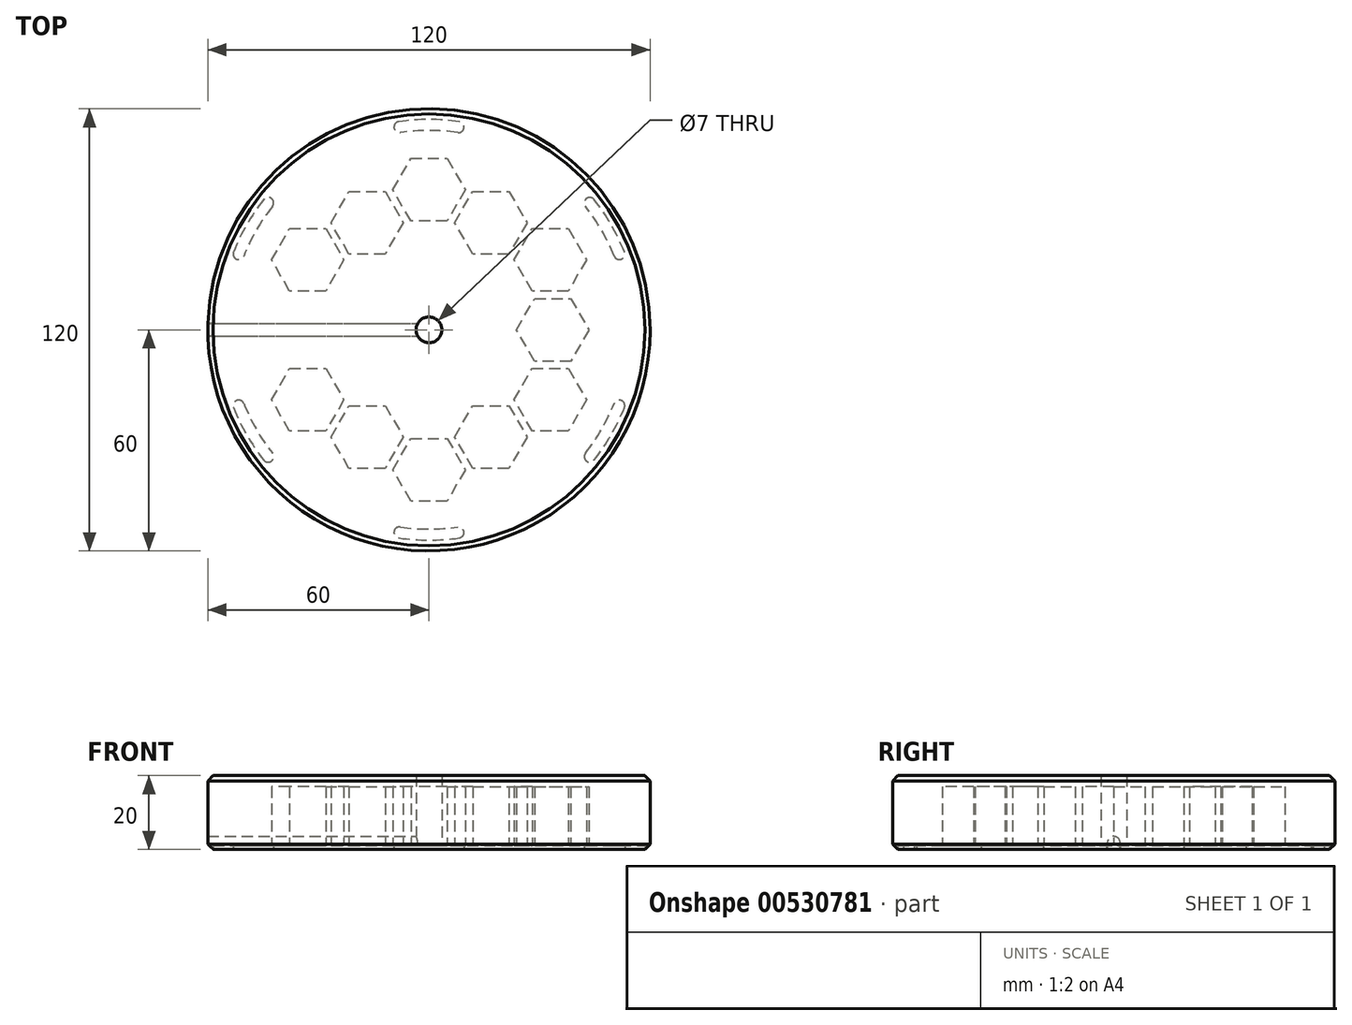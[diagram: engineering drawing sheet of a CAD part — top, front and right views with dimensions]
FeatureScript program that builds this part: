
annotation { "Feature Type Name" : "Feature", "Feature Type Description" : "" }
export const myFeature = defineFeature(function(context is Context, id is Id, definition is map)
    precondition{}
    {
        {
            var Q0;
            Q0=qCreatedBy(makeId("Top.planeOp"),FACE);
            var sketch = newSketch(context, id + "F0", { "sketchPlane" : qUnion([Q0])});
            skCircle(sketch, "E0", {"center": v(0, 0) * mm, "radius": 60 * mm});
            skCircle(sketch, "E1.cCircle", {"center": v(0, 38) * mm, "radius": 8.5 * mm, "construction": true});
            skLineSegment(sketch, "E1.0", {"start": v(4.9, 29.5) * mm, "end": v(-4.9, 29.5) * mm});
            skLineSegment(sketch, "E1.1", {"start": v(-4.9, 29.5) * mm, "end": v(-9.81, 38) * mm});
            skLineSegment(sketch, "E1.2", {"start": v(-9.81, 38) * mm, "end": v(-4.9, 46.5) * mm});
            skLineSegment(sketch, "E1.3", {"start": v(-4.9, 46.5) * mm, "end": v(4.9, 46.5) * mm});
            skLineSegment(sketch, "E1.4", {"start": v(4.9, 46.5) * mm, "end": v(9.81, 38) * mm});
            skLineSegment(sketch, "E1.5", {"start": v(9.81, 38) * mm, "end": v(4.9, 29.5) * mm});
            skPoint(sketch, "E1.0.midPoint", {"position": v(0, 29.5) * mm});
            skLineSegment(sketch, "E2.1.0", {"start": v(-28, 10.5) * mm, "end": v(-37.82, 10.5) * mm});
            skLineSegment(sketch, "E2.1.1", {"start": v(-37.82, 10.5) * mm, "end": v(-42.72, 19) * mm});
            skLineSegment(sketch, "E2.1.2", {"start": v(-42.72, 19) * mm, "end": v(-37.82, 27.5) * mm});
            skLineSegment(sketch, "E2.1.3", {"start": v(-37.82, 27.5) * mm, "end": v(-28, 27.5) * mm});
            skLineSegment(sketch, "E2.1.4", {"start": v(-28, 27.5) * mm, "end": v(-23.1, 19) * mm});
            skLineSegment(sketch, "E2.1.5", {"start": v(-23.1, 19) * mm, "end": v(-28, 10.5) * mm});
            skLineSegment(sketch, "E2.2.0", {"start": v(-23.1, -19) * mm, "end": v(-28, -27.5) * mm});
            skLineSegment(sketch, "E2.2.1", {"start": v(-28, -27.5) * mm, "end": v(-37.82, -27.5) * mm});
            skLineSegment(sketch, "E2.2.2", {"start": v(-37.82, -27.5) * mm, "end": v(-42.72, -19) * mm});
            skLineSegment(sketch, "E2.2.3", {"start": v(-42.72, -19) * mm, "end": v(-37.82, -10.5) * mm});
            skLineSegment(sketch, "E2.2.4", {"start": v(-37.82, -10.5) * mm, "end": v(-28, -10.5) * mm});
            skLineSegment(sketch, "E2.2.5", {"start": v(-28, -10.5) * mm, "end": v(-23.1, -19) * mm});
            skLineSegment(sketch, "E2.3.0", {"start": v(4.9, -29.5) * mm, "end": v(9.81, -38) * mm});
            skLineSegment(sketch, "E2.3.1", {"start": v(9.81, -38) * mm, "end": v(4.9, -46.5) * mm});
            skLineSegment(sketch, "E2.3.2", {"start": v(4.9, -46.5) * mm, "end": v(-4.9, -46.5) * mm});
            skLineSegment(sketch, "E2.3.3", {"start": v(-4.9, -46.5) * mm, "end": v(-9.81, -38) * mm});
            skLineSegment(sketch, "E2.3.4", {"start": v(-9.81, -38) * mm, "end": v(-4.9, -29.5) * mm});
            skLineSegment(sketch, "E2.3.5", {"start": v(-4.9, -29.5) * mm, "end": v(4.9, -29.5) * mm});
            skLineSegment(sketch, "E2.4.0", {"start": v(28, -10.5) * mm, "end": v(37.82, -10.5) * mm});
            skLineSegment(sketch, "E2.4.1", {"start": v(37.82, -10.5) * mm, "end": v(42.72, -19) * mm});
            skLineSegment(sketch, "E2.4.2", {"start": v(42.72, -19) * mm, "end": v(37.82, -27.5) * mm});
            skLineSegment(sketch, "E2.4.3", {"start": v(37.82, -27.5) * mm, "end": v(28, -27.5) * mm});
            skLineSegment(sketch, "E2.4.4", {"start": v(28, -27.5) * mm, "end": v(23.1, -19) * mm});
            skLineSegment(sketch, "E2.4.5", {"start": v(23.1, -19) * mm, "end": v(28, -10.5) * mm});
            skLineSegment(sketch, "E2.5.0", {"start": v(23.1, 19) * mm, "end": v(28, 27.5) * mm});
            skLineSegment(sketch, "E2.5.1", {"start": v(28, 27.5) * mm, "end": v(37.82, 27.5) * mm});
            skLineSegment(sketch, "E2.5.2", {"start": v(37.82, 27.5) * mm, "end": v(42.72, 19) * mm});
            skLineSegment(sketch, "E2.5.3", {"start": v(42.72, 19) * mm, "end": v(37.82, 10.5) * mm});
            skLineSegment(sketch, "E2.5.4", {"start": v(37.82, 10.5) * mm, "end": v(28, 10.5) * mm});
            skLineSegment(sketch, "E2.5.5", {"start": v(28, 10.5) * mm, "end": v(23.1, 19) * mm});
            skCircle(sketch, "E3", {"center": v(0, 0) * mm, "radius": 3.5 * mm});
            skCircle(sketch, "E4.cCircle", {"center": v(-16.79, 29.08) * mm, "radius": 8.5 * mm, "construction": true});
            skLineSegment(sketch, "E4.0", {"start": v(-21.7, 37.58) * mm, "end": v(-11.88, 37.58) * mm});
            skLineSegment(sketch, "E4.1", {"start": v(-11.88, 37.58) * mm, "end": v(-6.97, 29.08) * mm});
            skLineSegment(sketch, "E4.2", {"start": v(-6.97, 29.08) * mm, "end": v(-11.88, 20.58) * mm});
            skLineSegment(sketch, "E4.3", {"start": v(-11.88, 20.58) * mm, "end": v(-21.7, 20.58) * mm});
            skLineSegment(sketch, "E4.4", {"start": v(-21.7, 20.58) * mm, "end": v(-26.6, 29.08) * mm});
            skLineSegment(sketch, "E4.5", {"start": v(-26.6, 29.08) * mm, "end": v(-21.7, 37.58) * mm});
            skPoint(sketch, "E4.0.midPoint", {"position": v(-16.79, 37.58) * mm});
            skLineSegment(sketch, "E5.1.0", {"start": v(11.88, 20.58) * mm, "end": v(6.97, 29.08) * mm});
            skLineSegment(sketch, "E5.1.1", {"start": v(21.7, 20.58) * mm, "end": v(11.88, 20.58) * mm});
            skLineSegment(sketch, "E5.1.2", {"start": v(26.6, 29.08) * mm, "end": v(21.7, 20.58) * mm});
            skLineSegment(sketch, "E5.1.3", {"start": v(21.7, 37.58) * mm, "end": v(26.6, 29.08) * mm});
            skLineSegment(sketch, "E5.1.4", {"start": v(11.88, 37.58) * mm, "end": v(21.7, 37.58) * mm});
            skLineSegment(sketch, "E5.1.5", {"start": v(6.97, 29.08) * mm, "end": v(11.88, 37.58) * mm});
            skLineSegment(sketch, "E5.2.0", {"start": v(23.76, 0) * mm, "end": v(28.67, 8.5) * mm});
            skLineSegment(sketch, "E5.2.1", {"start": v(28.67, -8.5) * mm, "end": v(23.76, 0) * mm});
            skLineSegment(sketch, "E5.2.2", {"start": v(38.49, -8.5) * mm, "end": v(28.67, -8.5) * mm});
            skLineSegment(sketch, "E5.2.3", {"start": v(43.4, 0) * mm, "end": v(38.49, -8.5) * mm});
            skLineSegment(sketch, "E5.2.4", {"start": v(38.49, 8.5) * mm, "end": v(43.4, 0) * mm});
            skLineSegment(sketch, "E5.2.5", {"start": v(28.67, 8.5) * mm, "end": v(38.49, 8.5) * mm});
            skLineSegment(sketch, "E5.3.0", {"start": v(11.88, -20.58) * mm, "end": v(21.7, -20.58) * mm});
            skLineSegment(sketch, "E5.3.1", {"start": v(6.97, -29.08) * mm, "end": v(11.88, -20.58) * mm});
            skLineSegment(sketch, "E5.3.2", {"start": v(11.88, -37.58) * mm, "end": v(6.97, -29.08) * mm});
            skLineSegment(sketch, "E5.3.3", {"start": v(21.7, -37.58) * mm, "end": v(11.88, -37.58) * mm});
            skLineSegment(sketch, "E5.3.4", {"start": v(26.6, -29.08) * mm, "end": v(21.7, -37.58) * mm});
            skLineSegment(sketch, "E5.3.5", {"start": v(21.7, -20.58) * mm, "end": v(26.6, -29.08) * mm});
            skLineSegment(sketch, "E5.4.0", {"start": v(-11.88, -20.58) * mm, "end": v(-6.97, -29.08) * mm});
            skLineSegment(sketch, "E5.4.1", {"start": v(-21.7, -20.58) * mm, "end": v(-11.88, -20.58) * mm});
            skLineSegment(sketch, "E5.4.2", {"start": v(-26.6, -29.08) * mm, "end": v(-21.7, -20.58) * mm});
            skLineSegment(sketch, "E5.4.3", {"start": v(-21.7, -37.58) * mm, "end": v(-26.6, -29.08) * mm});
            skLineSegment(sketch, "E5.4.4", {"start": v(-11.88, -37.58) * mm, "end": v(-21.7, -37.58) * mm});
            skLineSegment(sketch, "E5.4.5", {"start": v(-6.97, -29.08) * mm, "end": v(-11.88, -37.58) * mm});
            skLineSegment(sketch, "E5.anchor1", {"start": v(0, 0) * mm, "end": v(-21.7, 20.58) * mm, "construction": true});
            skLineSegment(sketch, "E5.anchor2", {"start": v(0, 0) * mm, "end": v(-6.97, -29.08) * mm, "construction": true});
            skLineSegment(sketch, "E6", {"start": v(0, 0) * mm, "end": v(-4.9, 29.5) * mm, "construction": true});
            skSolve(sketch);
        }
        {
            var Q0;
            Q0=makeQuery(id+"F0.imprint","IMPRINT",FACE,{"disambiguationData":[TD([[makeQuery(id+"F0.imprint","IMPRINT",EDGE,{"derivedFrom":sQuery(id+"F0.wireOp",EDGE,"E0")}),1.0]])]});
            extrude(context, id + "F1", {"entities" : qUnion([Q0]), "depth" : 20 * mm, "offsetDistance" : 25 * mm});
        }
        {
            var Q0;
            Q0=makeQuery(id+"F0.imprint","IMPRINT",FACE,{"disambiguationData":[TD([[makeQuery(id+"F0.imprint","IMPRINT",EDGE,{"derivedFrom":sQuery(id+"F0.wireOp",EDGE,"E2.1.0")}),-1.0]])]});
            var Q1;
            Q1=makeQuery(id+"F0.imprint","IMPRINT",FACE,{"disambiguationData":[TD([[makeQuery(id+"F0.imprint","IMPRINT",EDGE,{"derivedFrom":sQuery(id+"F0.wireOp",EDGE,"E1.0")}),-1.0]])]});
            var Q2;
            Q2=makeQuery(id+"F0.imprint","IMPRINT",FACE,{"disambiguationData":[TD([[makeQuery(id+"F0.imprint","IMPRINT",EDGE,{"derivedFrom":sQuery(id+"F0.wireOp",EDGE,"E2.5.0")}),-1.0]])]});
            var Q3;
            Q3=makeQuery(id+"F0.imprint","IMPRINT",FACE,{"disambiguationData":[TD([[makeQuery(id+"F0.imprint","IMPRINT",EDGE,{"derivedFrom":sQuery(id+"F0.wireOp",EDGE,"E2.4.0")}),-1.0]])]});
            var Q4;
            Q4=makeQuery(id+"F0.imprint","IMPRINT",FACE,{"disambiguationData":[TD([[makeQuery(id+"F0.imprint","IMPRINT",EDGE,{"derivedFrom":sQuery(id+"F0.wireOp",EDGE,"E2.3.0")}),-1.0]])]});
            var Q5;
            Q5=makeQuery(id+"F0.imprint","IMPRINT",FACE,{"disambiguationData":[TD([[makeQuery(id+"F0.imprint","IMPRINT",EDGE,{"derivedFrom":sQuery(id+"F0.wireOp",EDGE,"E2.2.0")}),-1.0]])]});
            var Q6;
            Q6=makeQuery(id+"F0.imprint","IMPRINT",FACE,{"disambiguationData":[TD([[makeQuery(id+"F0.imprint","IMPRINT",EDGE,{"derivedFrom":sQuery(id+"F0.wireOp",EDGE,"E5.4.0")}),-1.0]])]});
            var Q7;
            Q7=makeQuery(id+"F0.imprint","IMPRINT",FACE,{"disambiguationData":[TD([[makeQuery(id+"F0.imprint","IMPRINT",EDGE,{"derivedFrom":sQuery(id+"F0.wireOp",EDGE,"E5.3.0")}),-1.0]])]});
            var Q8;
            Q8=makeQuery(id+"F0.imprint","IMPRINT",FACE,{"disambiguationData":[TD([[makeQuery(id+"F0.imprint","IMPRINT",EDGE,{"derivedFrom":sQuery(id+"F0.wireOp",EDGE,"E5.2.0")}),-1.0]])]});
            var Q9;
            Q9=makeQuery(id+"F0.imprint","IMPRINT",FACE,{"disambiguationData":[TD([[makeQuery(id+"F0.imprint","IMPRINT",EDGE,{"derivedFrom":sQuery(id+"F0.wireOp",EDGE,"E5.1.0")}),-1.0]])]});
            var Q10;
            Q10=makeQuery(id+"F0.imprint","IMPRINT",FACE,{"disambiguationData":[TD([[makeQuery(id+"F0.imprint","IMPRINT",EDGE,{"derivedFrom":sQuery(id+"F0.wireOp",EDGE,"E4.0")}),-1.0]])]});
            var Q11;
            Q11=makeQuery(id+"F1.opExtrude","CAP_FACE",FACE,{"disambiguationData":[OSD([sQuery(id+"F0.wireOp",EDGE,"E0"),sQuery(id+"F0.wireOp",EDGE,"E1.0"),sQuery(id+"F0.wireOp",EDGE,"E1.1"),sQuery(id+"F0.wireOp",EDGE,"E1.2"),sQuery(id+"F0.wireOp",EDGE,"E1.3"),sQuery(id+"F0.wireOp",EDGE,"E1.4"),sQuery(id+"F0.wireOp",EDGE,"E1.5"),sQuery(id+"F0.wireOp",EDGE,"E2.1.0"),sQuery(id+"F0.wireOp",EDGE,"E2.1.1"),sQuery(id+"F0.wireOp",EDGE,"E2.1.2"),sQuery(id+"F0.wireOp",EDGE,"E2.1.3"),sQuery(id+"F0.wireOp",EDGE,"E2.1.4"),sQuery(id+"F0.wireOp",EDGE,"E2.1.5"),sQuery(id+"F0.wireOp",EDGE,"E2.2.0"),sQuery(id+"F0.wireOp",EDGE,"E2.2.1"),sQuery(id+"F0.wireOp",EDGE,"E2.2.2"),sQuery(id+"F0.wireOp",EDGE,"E2.2.3"),sQuery(id+"F0.wireOp",EDGE,"E2.2.4"),sQuery(id+"F0.wireOp",EDGE,"E2.2.5"),sQuery(id+"F0.wireOp",EDGE,"E2.3.0"),sQuery(id+"F0.wireOp",EDGE,"E2.3.1"),sQuery(id+"F0.wireOp",EDGE,"E2.3.2"),sQuery(id+"F0.wireOp",EDGE,"E2.3.3"),sQuery(id+"F0.wireOp",EDGE,"E2.3.4"),sQuery(id+"F0.wireOp",EDGE,"E2.3.5"),sQuery(id+"F0.wireOp",EDGE,"E2.4.0"),sQuery(id+"F0.wireOp",EDGE,"E2.4.1"),sQuery(id+"F0.wireOp",EDGE,"E2.4.2"),sQuery(id+"F0.wireOp",EDGE,"E2.4.3"),sQuery(id+"F0.wireOp",EDGE,"E2.4.4"),sQuery(id+"F0.wireOp",EDGE,"E2.4.5"),sQuery(id+"F0.wireOp",EDGE,"E2.5.0"),sQuery(id+"F0.wireOp",EDGE,"E2.5.1"),sQuery(id+"F0.wireOp",EDGE,"E2.5.2"),sQuery(id+"F0.wireOp",EDGE,"E2.5.3"),sQuery(id+"F0.wireOp",EDGE,"E2.5.4"),sQuery(id+"F0.wireOp",EDGE,"E2.5.5"),sQuery(id+"F0.wireOp",EDGE,"E3")])],"isStart":false});
            extrude(context, id + "F2", {"entities" : qUnion([Q0, Q1, Q2, Q3, Q4, Q5, Q6, Q7, Q8, Q9, Q10]), "operationType" : NewBodyOperationType.ADD, "endBound" : BoundingType.UP_TO_SURFACE, "depth" : 25 * mm, "endBoundEntityFace" : qUnion([Q11]), "offsetDistance" : 25 * mm, "hasSecondDirection" : true, "secondDirectionOppositeDirection" : false, "secondDirectionDepth" : 17 * mm});
        }
        {
            var Q0;
            Q0=makeQuery(id+"F1.opExtrude","CAP_EDGE",EDGE,{"disambiguationData":[OSD([sQuery(id+"F0.wireOp",EDGE,"E0")])],"isStart":false});
            chamfer(context, id + "F3", {"entities" : qUnion([Q0]), "width" : 1.41 * mm, "tangentPropagation" : true});
        }
        {
            var Q0;
            Q0=makeQuery(id+"F1.opExtrude","CAP_EDGE",EDGE,{"disambiguationData":[OSD([sQuery(id+"F0.wireOp",EDGE,"E0")])],"isStart":true});
            chamfer(context, id + "F4", {"entities" : qUnion([Q0]), "width" : 1.41 * mm, "tangentPropagation" : true});
        }
        {
            var Q0;
            Q0=qCreatedBy(makeId("Right.planeOp"),FACE);
            var sketch = newSketch(context, id + "F5", { "sketchPlane" : qUnion([Q0])});
            skCircle(sketch, "E7", {"center": v(0, 1.75) * mm, "radius": 1.75 * mm});
            skLineSegment(sketch, "E8.bottom", {"start": v(-1.75, 1.75) * mm, "end": v(1.75, 1.75) * mm});
            skLineSegment(sketch, "E8.top", {"start": v(-1.75, -1.75) * mm, "end": v(1.75, -1.75) * mm});
            skLineSegment(sketch, "E8.left", {"start": v(-1.75, 1.75) * mm, "end": v(-1.75, -1.75) * mm});
            skLineSegment(sketch, "E8.right", {"start": v(1.75, 1.75) * mm, "end": v(1.75, -1.75) * mm});
            skSolve(sketch);
        }
        {
            var Q0;
            Q0 = qSketchRegion(id + "F5", true);
            extrude(context, id + "F6", {"entities" : qUnion([Q0]), "operationType" : NewBodyOperationType.REMOVE, "oppositeDirection" : true, "depth" : 150 * mm, "offsetDistance" : 25 * mm});
        }
        {
            var Q0;
            Q0=makeQuery(id+"F1.opExtrude","CAP_FACE",FACE,{"disambiguationData":[OSD([sQuery(id+"F0.wireOp",EDGE,"E0"),sQuery(id+"F0.wireOp",EDGE,"E1.0"),sQuery(id+"F0.wireOp",EDGE,"E1.1"),sQuery(id+"F0.wireOp",EDGE,"E1.2"),sQuery(id+"F0.wireOp",EDGE,"E1.3"),sQuery(id+"F0.wireOp",EDGE,"E1.4"),sQuery(id+"F0.wireOp",EDGE,"E1.5"),sQuery(id+"F0.wireOp",EDGE,"E2.1.0"),sQuery(id+"F0.wireOp",EDGE,"E2.1.1"),sQuery(id+"F0.wireOp",EDGE,"E2.1.2"),sQuery(id+"F0.wireOp",EDGE,"E2.1.3"),sQuery(id+"F0.wireOp",EDGE,"E2.1.4"),sQuery(id+"F0.wireOp",EDGE,"E2.1.5"),sQuery(id+"F0.wireOp",EDGE,"E2.2.0"),sQuery(id+"F0.wireOp",EDGE,"E2.2.1"),sQuery(id+"F0.wireOp",EDGE,"E2.2.2"),sQuery(id+"F0.wireOp",EDGE,"E2.2.3"),sQuery(id+"F0.wireOp",EDGE,"E2.2.4"),sQuery(id+"F0.wireOp",EDGE,"E2.2.5"),sQuery(id+"F0.wireOp",EDGE,"E2.3.0"),sQuery(id+"F0.wireOp",EDGE,"E2.3.1"),sQuery(id+"F0.wireOp",EDGE,"E2.3.2"),sQuery(id+"F0.wireOp",EDGE,"E2.3.3"),sQuery(id+"F0.wireOp",EDGE,"E2.3.4"),sQuery(id+"F0.wireOp",EDGE,"E2.3.5"),sQuery(id+"F0.wireOp",EDGE,"E2.4.0"),sQuery(id+"F0.wireOp",EDGE,"E2.4.1"),sQuery(id+"F0.wireOp",EDGE,"E2.4.2"),sQuery(id+"F0.wireOp",EDGE,"E2.4.3"),sQuery(id+"F0.wireOp",EDGE,"E2.4.4"),sQuery(id+"F0.wireOp",EDGE,"E2.4.5"),sQuery(id+"F0.wireOp",EDGE,"E2.5.0"),sQuery(id+"F0.wireOp",EDGE,"E2.5.1"),sQuery(id+"F0.wireOp",EDGE,"E2.5.2"),sQuery(id+"F0.wireOp",EDGE,"E2.5.3"),sQuery(id+"F0.wireOp",EDGE,"E2.5.4"),sQuery(id+"F0.wireOp",EDGE,"E2.5.5"),sQuery(id+"F0.wireOp",EDGE,"E3"),sQuery(id+"F0.wireOp",EDGE,"E4.0"),sQuery(id+"F0.wireOp",EDGE,"E4.1"),sQuery(id+"F0.wireOp",EDGE,"E4.2"),sQuery(id+"F0.wireOp",EDGE,"E4.3"),sQuery(id+"F0.wireOp",EDGE,"E4.4"),sQuery(id+"F0.wireOp",EDGE,"E4.5"),sQuery(id+"F0.wireOp",EDGE,"E5.1.0"),sQuery(id+"F0.wireOp",EDGE,"E5.1.1"),sQuery(id+"F0.wireOp",EDGE,"E5.1.2"),sQuery(id+"F0.wireOp",EDGE,"E5.1.3"),sQuery(id+"F0.wireOp",EDGE,"E5.1.4"),sQuery(id+"F0.wireOp",EDGE,"E5.1.5"),sQuery(id+"F0.wireOp",EDGE,"E5.2.0"),sQuery(id+"F0.wireOp",EDGE,"E5.2.1"),sQuery(id+"F0.wireOp",EDGE,"E5.2.2"),sQuery(id+"F0.wireOp",EDGE,"E5.2.3"),sQuery(id+"F0.wireOp",EDGE,"E5.2.4"),sQuery(id+"F0.wireOp",EDGE,"E5.2.5"),sQuery(id+"F0.wireOp",EDGE,"E5.3.0"),sQuery(id+"F0.wireOp",EDGE,"E5.3.1"),sQuery(id+"F0.wireOp",EDGE,"E5.3.2"),sQuery(id+"F0.wireOp",EDGE,"E5.3.3"),sQuery(id+"F0.wireOp",EDGE,"E5.3.4"),sQuery(id+"F0.wireOp",EDGE,"E5.3.5"),sQuery(id+"F0.wireOp",EDGE,"E5.4.0"),sQuery(id+"F0.wireOp",EDGE,"E5.4.1"),sQuery(id+"F0.wireOp",EDGE,"E5.4.2"),sQuery(id+"F0.wireOp",EDGE,"E5.4.3"),sQuery(id+"F0.wireOp",EDGE,"E5.4.4"),sQuery(id+"F0.wireOp",EDGE,"E5.4.5")])],"isStart":true});
            var sketch = newSketch(context, id + "F7", { "sketchPlane" : qUnion([Q0])});
            skArc(sketch, "E9", {"start": v(-8, 55) * mm, "mid": v(0, 55.59) * mm, "end": v(8, 55) * mm, "construction": true});
            skArc(sketch, "E10.0.startCap", {"start": v(-7.78, 53.52) * mm, "mid": v(-9.48, 54.8) * mm, "end": v(-8.22, 56.5) * mm});
            skArc(sketch, "E10.0.endCap", {"start": v(8.22, 56.5) * mm, "mid": v(9.48, 54.8) * mm, "end": v(7.78, 53.52) * mm});
            skArc(sketch, "E10.0.left", {"start": v(-8.22, 56.5) * mm, "mid": v(0, 57.09) * mm, "end": v(8.22, 56.5) * mm});
            skArc(sketch, "E10.0.right", {"start": v(-7.78, 53.52) * mm, "mid": v(0, 54.09) * mm, "end": v(7.78, 53.52) * mm});
            skArc(sketch, "E11.1.0", {"start": v(-50.24, 20.02) * mm, "mid": v(-46.84, 27.04) * mm, "end": v(-42.46, 33.5) * mm});
            skArc(sketch, "E11.1.1", {"start": v(-53.03, 21.13) * mm, "mid": v(-49.44, 28.54) * mm, "end": v(-44.82, 35.36) * mm});
            skArc(sketch, "E11.1.2", {"start": v(-44.82, 35.36) * mm, "mid": v(-42.7, 35.6) * mm, "end": v(-42.46, 33.5) * mm});
            skArc(sketch, "E11.1.3", {"start": v(-50.24, 20.02) * mm, "mid": v(-52.2, 19.18) * mm, "end": v(-53.03, 21.13) * mm});
            skArc(sketch, "E11.2.0", {"start": v(-42.46, -33.5) * mm, "mid": v(-46.84, -27.04) * mm, "end": v(-50.24, -20.02) * mm});
            skArc(sketch, "E11.2.1", {"start": v(-44.82, -35.36) * mm, "mid": v(-49.44, -28.54) * mm, "end": v(-53.03, -21.13) * mm});
            skArc(sketch, "E11.2.2", {"start": v(-53.03, -21.13) * mm, "mid": v(-52.2, -19.18) * mm, "end": v(-50.24, -20.02) * mm});
            skArc(sketch, "E11.2.3", {"start": v(-42.46, -33.5) * mm, "mid": v(-42.7, -35.6) * mm, "end": v(-44.82, -35.36) * mm});
            skArc(sketch, "E11.3.0", {"start": v(7.78, -53.52) * mm, "mid": v(0, -54.09) * mm, "end": v(-7.78, -53.52) * mm});
            skArc(sketch, "E11.3.1", {"start": v(8.22, -56.5) * mm, "mid": v(0, -57.09) * mm, "end": v(-8.22, -56.5) * mm});
            skArc(sketch, "E11.3.2", {"start": v(-8.22, -56.5) * mm, "mid": v(-9.48, -54.8) * mm, "end": v(-7.78, -53.52) * mm});
            skArc(sketch, "E11.3.3", {"start": v(7.78, -53.52) * mm, "mid": v(9.48, -54.8) * mm, "end": v(8.22, -56.5) * mm});
            skArc(sketch, "E11.4.0", {"start": v(50.24, -20.02) * mm, "mid": v(46.84, -27.04) * mm, "end": v(42.46, -33.5) * mm});
            skArc(sketch, "E11.4.1", {"start": v(53.03, -21.13) * mm, "mid": v(49.44, -28.54) * mm, "end": v(44.82, -35.36) * mm});
            skArc(sketch, "E11.4.2", {"start": v(44.82, -35.36) * mm, "mid": v(42.7, -35.6) * mm, "end": v(42.46, -33.5) * mm});
            skArc(sketch, "E11.4.3", {"start": v(50.24, -20.02) * mm, "mid": v(52.2, -19.18) * mm, "end": v(53.03, -21.13) * mm});
            skArc(sketch, "E11.5.0", {"start": v(42.46, 33.5) * mm, "mid": v(46.84, 27.04) * mm, "end": v(50.24, 20.02) * mm});
            skArc(sketch, "E11.5.1", {"start": v(44.82, 35.36) * mm, "mid": v(49.44, 28.54) * mm, "end": v(53.03, 21.13) * mm});
            skArc(sketch, "E11.5.2", {"start": v(53.03, 21.13) * mm, "mid": v(52.2, 19.18) * mm, "end": v(50.24, 20.02) * mm});
            skArc(sketch, "E11.5.3", {"start": v(42.46, 33.5) * mm, "mid": v(42.7, 35.6) * mm, "end": v(44.82, 35.36) * mm});
            skPoint(sketch, "E12", {"position": v(0, 55.59) * mm});
            skSolve(sketch);
        }
        {
            var Q0;
            Q0=makeQuery(id+"F7.imprint","IMPRINT",FACE,{"disambiguationData":[TD([[makeQuery(id+"F7.imprint","IMPRINT",EDGE,{"derivedFrom":sQuery(id+"F7.wireOp",EDGE,"E11.2.0")}),1.0]])]});
            var Q1;
            Q1=makeQuery(id+"F7.imprint","IMPRINT",FACE,{"disambiguationData":[TD([[makeQuery(id+"F7.imprint","IMPRINT",EDGE,{"derivedFrom":sQuery(id+"F7.wireOp",EDGE,"E11.1.0")}),1.0]])]});
            var Q2;
            Q2=makeQuery(id+"F7.imprint","IMPRINT",FACE,{"disambiguationData":[TD([[makeQuery(id+"F7.imprint","IMPRINT",EDGE,{"derivedFrom":sQuery(id+"F7.wireOp",EDGE,"E10.0.startCap")}),-1.0]])]});
            var Q3;
            Q3=makeQuery(id+"F7.imprint","IMPRINT",FACE,{"disambiguationData":[TD([[makeQuery(id+"F7.imprint","IMPRINT",EDGE,{"derivedFrom":sQuery(id+"F7.wireOp",EDGE,"E11.5.0")}),1.0]])]});
            var Q4;
            Q4=makeQuery(id+"F7.imprint","IMPRINT",FACE,{"disambiguationData":[TD([[makeQuery(id+"F7.imprint","IMPRINT",EDGE,{"derivedFrom":sQuery(id+"F7.wireOp",EDGE,"E11.4.0")}),1.0]])]});
            var Q5;
            Q5=makeQuery(id+"F7.imprint","IMPRINT",FACE,{"disambiguationData":[TD([[makeQuery(id+"F7.imprint","IMPRINT",EDGE,{"derivedFrom":sQuery(id+"F7.wireOp",EDGE,"E11.3.0")}),1.0]])]});
            extrude(context, id + "F8", {"entities" : qUnion([Q0, Q1, Q2, Q3, Q4, Q5]), "operationType" : NewBodyOperationType.REMOVE, "oppositeDirection" : true, "depth" : 1 * mm, "offsetDistance" : 25 * mm});
        }
    });
